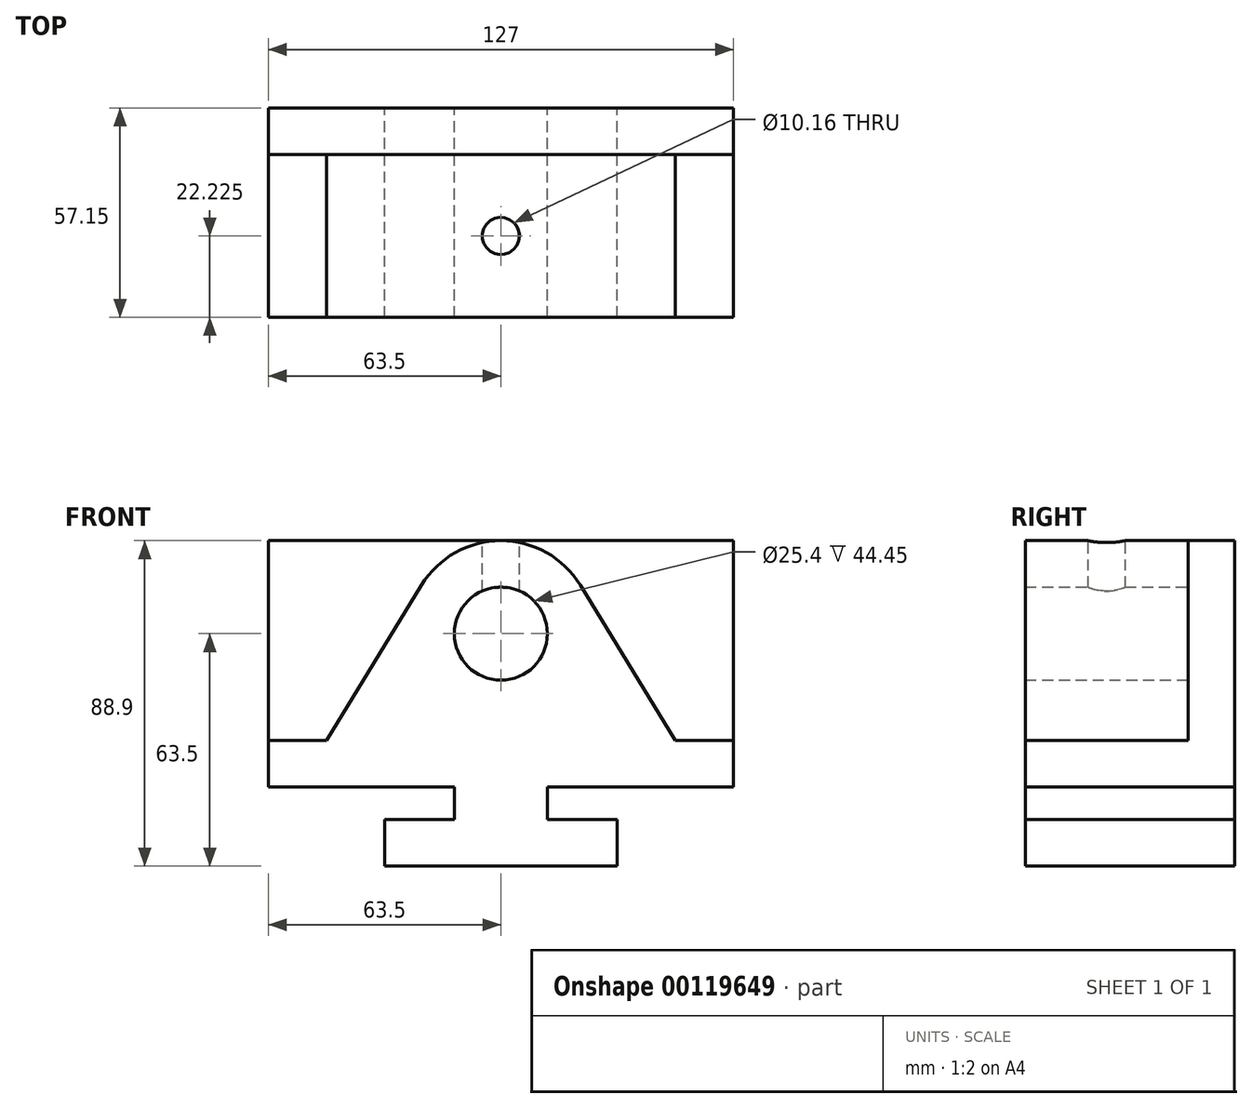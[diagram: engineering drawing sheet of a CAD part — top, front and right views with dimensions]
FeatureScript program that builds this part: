
annotation { "Feature Type Name" : "Feature", "Feature Type Description" : "" }
export const myFeature = defineFeature(function(context is Context, id is Id, definition is map)
    precondition{}
    {
        {
            var Q0;
            Q0=qCreatedBy(makeId("Front.planeOp"),FACE);
            var sketch = newSketch(context, id + "F0", { "sketchPlane" : qUnion([Q0])});
            skLineSegment(sketch, "E0", {"start": v(-31.75, 0) * mm, "end": v(31.75, 0) * mm});
            skLineSegment(sketch, "E1", {"start": v(31.75, 0) * mm, "end": v(31.75, 12.7) * mm});
            skLineSegment(sketch, "E2", {"start": v(31.75, 12.7) * mm, "end": v(12.7, 12.7) * mm});
            skLineSegment(sketch, "E3", {"start": v(12.7, 12.7) * mm, "end": v(12.7, 21.59) * mm});
            skLineSegment(sketch, "E4", {"start": v(12.7, 21.59) * mm, "end": v(63.5, 21.59) * mm});
            skLineSegment(sketch, "E5", {"start": v(63.5, 21.6) * mm, "end": v(63.5, 34.3) * mm});
            skLineSegment(sketch, "E6", {"start": v(63.5, 34.3) * mm, "end": v(47.62, 34.3) * mm});
            skLineSegment(sketch, "E7", {"start": v(47.62, 34.29) * mm, "end": v(21.67, 76.75) * mm});
            skLineSegment(sketch, "E8", {"start": v(-31.75, 0) * mm, "end": v(-31.75, 12.7) * mm});
            skLineSegment(sketch, "E9", {"start": v(-31.75, 12.7) * mm, "end": v(-12.7, 12.7) * mm});
            skLineSegment(sketch, "E10", {"start": v(-12.7, 12.7) * mm, "end": v(-12.7, 21.6) * mm});
            skLineSegment(sketch, "E11", {"start": v(-12.7, 21.6) * mm, "end": v(-63.5, 21.59) * mm});
            skLineSegment(sketch, "E12", {"start": v(-63.5, 21.59) * mm, "end": v(-63.5, 34.3) * mm});
            skLineSegment(sketch, "E13", {"start": v(-63.5, 34.3) * mm, "end": v(-47.62, 34.3) * mm});
            skLineSegment(sketch, "E14", {"start": v(-47.62, 34.3) * mm, "end": v(-21.67, 76.75) * mm});
            skArc(sketch, "E15", {"start": v(21.67, 76.75) * mm, "mid": v(0, 88.9) * mm, "end": v(-21.67, 76.75) * mm});
            skLineSegment(sketch, "E16", {"start": v(0, 0) * mm, "end": v(0, 105.2) * mm, "construction": true});
            skCircle(sketch, "E17", {"center": v(0, 63.5) * mm, "radius": 12.7 * mm});
            skSolve(sketch);
        }
        {
            var Q0;
            Q0 = qSketchRegion(id + "F0", true);
            extrude(context, id + "F1", {"entities" : qUnion([Q0]), "depth" : 44.45 * mm});
        }
        {
            var Q0;
            Q0=makeQuery(id+"F1.opExtrude","CAP_FACE",FACE,{"disambiguationData":[OSD([sQuery(id+"F0.wireOp",EDGE,"E0"),sQuery(id+"F0.wireOp",EDGE,"E1"),sQuery(id+"F0.wireOp",EDGE,"E2"),sQuery(id+"F0.wireOp",EDGE,"E3"),sQuery(id+"F0.wireOp",EDGE,"E4"),sQuery(id+"F0.wireOp",EDGE,"E5"),sQuery(id+"F0.wireOp",EDGE,"E6"),sQuery(id+"F0.wireOp",EDGE,"E7"),sQuery(id+"F0.wireOp",EDGE,"E8"),sQuery(id+"F0.wireOp",EDGE,"E9"),sQuery(id+"F0.wireOp",EDGE,"E10"),sQuery(id+"F0.wireOp",EDGE,"E11"),sQuery(id+"F0.wireOp",EDGE,"E12"),sQuery(id+"F0.wireOp",EDGE,"E13"),sQuery(id+"F0.wireOp",EDGE,"E14"),sQuery(id+"F0.wireOp",EDGE,"E15"),sQuery(id+"F0.wireOp",EDGE,"E17")])],"isStart":true});
            var sketch = newSketch(context, id + "F2", { "sketchPlane" : qUnion([Q0])});
            skLineSegment(sketch, "E18.bottom", {"start": v(-63.5, 21.6) * mm, "end": v(63.5, 21.6) * mm});
            skLineSegment(sketch, "E18.top", {"start": v(-63.5, 88.9) * mm, "end": v(63.5, 88.9) * mm});
            skLineSegment(sketch, "E18.left", {"start": v(-63.5, 21.6) * mm, "end": v(-63.5, 88.9) * mm});
            skLineSegment(sketch, "E18.right", {"start": v(63.5, 21.59) * mm, "end": v(63.5, 88.9) * mm});
            skSolve(sketch);
        }
        {
            var Q0;
            Q0 = qSketchRegion(id + "F2", true);
            var Q1;
            Q1=makeQuery(id+"F2.imprint","IMPRINT",FACE,{"disambiguationData":[TD([[makeQuery(id+"F2.imprint","IMPRINT",EDGE,{"derivedFrom":makeQuery(id+"F1.opExtrude","CAP_EDGE",EDGE,{"disambiguationData":[OSD([sQuery(id+"F0.wireOp",EDGE,"E0")])],"isStart":true})}),-1.0]])]});
            extrude(context, id + "F3", {"entities" : qUnion([Q0, Q1]), "operationType" : NewBodyOperationType.ADD, "depth" : 12.7 * mm});
        }
        {
            var Q0;
            Q0=makeQuery(id+"F3.opExtrude","SWEPT_FACE",FACE,{"disambiguationData":[OSD([sQuery(id+"F2.wireOp",EDGE,"E18.top")])]});
            var sketch = newSketch(context, id + "F4", { "sketchPlane" : qUnion([Q0])});
            skLineSegment(sketch, "E19", {"start": v(0, 37.16) * mm, "end": v(0, -70.21) * mm, "construction": true});
            skCircle(sketch, "E20", {"center": v(0, -22.23) * mm, "radius": 5.08 * mm});
            skSolve(sketch);
        }
        {
            var Q0;
            Q0 = qSketchRegion(id + "F4", true);
            extrude(context, id + "F5", {"entities" : qUnion([Q0]), "operationType" : NewBodyOperationType.REMOVE, "endBound" : BoundingType.UP_TO_NEXT, "oppositeDirection" : true, "depth" : 25.4 * mm});
        }
    });
